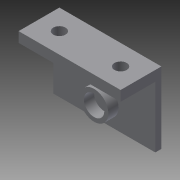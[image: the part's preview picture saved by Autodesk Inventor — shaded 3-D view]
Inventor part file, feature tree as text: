
AUTODESK INVENTOR PART (.ipt)
format: ipt  version: 2014 SP1 (Build 180222100, 222)  size: 131,072 bytes
history: native  units: mm
features: extrude x3, sketch x3
ambient origin geometry x8: Origin, YZ Plane, XZ Plane, XY Plane, X Axis, Y Axis, Z Axis, Center Point
bodies: Body1 (feature_tree)
feature tree (6):
  extrude  "Extrusion5"  Depth=20.0mm
  extrude  "Extrusion6"  Depth=6.0mm
  extrude  "Extrusion8"  Depth=10.0mm
  sketch  "Sketch5"  dims[d43=50.0mm d44=20.0mm]
  sketch  "Sketch8"  dims[d47=6.0mm d48=6.0mm]
  sketch  "Sketch10"  dims[d49=10.0mm d50=10.0mm d51=10.0mm d52=10.0mm d53=5.0mm d54=0.0mm d55=50.0mm d56=35.0mm d59=3.0mm d60=0.0mm d68=20.0mm d69=10.0mm d70=14.0mm d71=5.0mm d72=0.0mm]
